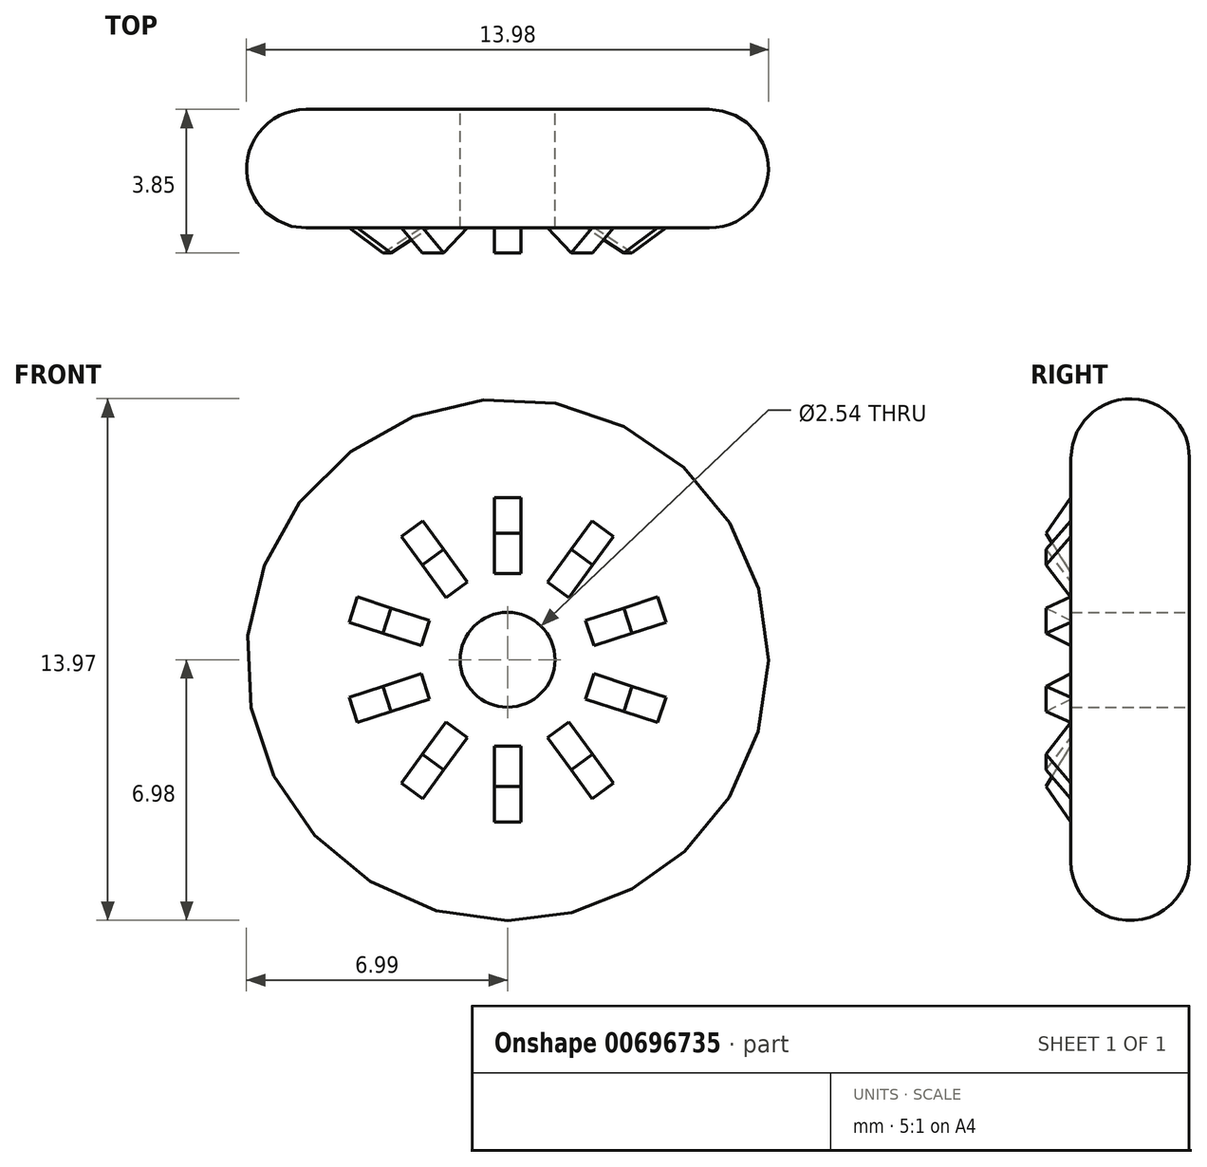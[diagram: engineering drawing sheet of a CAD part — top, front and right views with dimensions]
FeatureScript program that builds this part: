
annotation { "Feature Type Name" : "Feature", "Feature Type Description" : "" }
export const myFeature = defineFeature(function(context is Context, id is Id, definition is map)
    precondition{}
    {
        {
            var Q0;
            Q0=qCreatedBy(makeId("Front.planeOp"),FACE);
            var sketch = newSketch(context, id + "F0", { "sketchPlane" : qUnion([Q0])});
            skCircle(sketch, "E0", {"center": v(0, 0) * mm, "radius": 1.27 * mm});
            skCircle(sketch, "E1", {"center": v(0, 0) * mm, "radius": 6.99 * mm});
            skSolve(sketch);
        }
        {
            var Q0;
            Q0=makeQuery(id+"F0.imprint","IMPRINT",FACE,{"disambiguationData":[TD([[makeQuery(id+"F0.imprint","IMPRINT",EDGE,{"derivedFrom":sQuery(id+"F0.wireOp",EDGE,"E0")}),-1.0]])]});
            extrude(context, id + "F1", {"entities" : qUnion([Q0]), "endBound" : BoundingType.SYMMETRIC, "depth" : 3.17 * mm, "offsetDistance" : 25.4 * mm});
        }
        {
            var Q0;
            Q0=makeQuery(id+"F1.opExtrude","CAP_EDGE",EDGE,{"disambiguationData":[OSD([sQuery(id+"F0.wireOp",EDGE,"E1")])],"isStart":true});
            var Q1;
            Q1=makeQuery(id+"F1.opExtrude","CAP_EDGE",EDGE,{"disambiguationData":[OSD([sQuery(id+"F0.wireOp",EDGE,"E1")])],"isStart":false});
            fillet(context, id + "F2", {"entities" : qUnion([Q0, Q1]), "radius" : 1.59 * mm, "tangentPropagation" : true, "allowEdgeOverflow" : false});
        }
        {
            var Q0;
            Q0=qCreatedBy(makeId("Right.planeOp"),FACE);
            var sketch = newSketch(context, id + "F3", { "sketchPlane" : qUnion([Q0])});
            skLineSegment(sketch, "E2", {"start": v(-1.5, 4.48) * mm, "end": v(-2.26, 3.4) * mm});
            skLineSegment(sketch, "E3", {"start": v(-2.26, 3.4) * mm, "end": v(-1.58, 2.3) * mm});
            skLineSegment(sketch, "E4", {"start": v(-1.58, 2.3) * mm, "end": v(-1.5, 4.48) * mm});
            skPoint(sketch, "E5", {"position": v(-1.54, 3.4) * mm});
            skSolve(sketch);
        }
        {
            var Q0;
            Q0 = qSketchRegion(id + "F3", true);
            extrude(context, id + "F4", {"entities" : qUnion([Q0]), "operationType" : NewBodyOperationType.ADD, "endBound" : BoundingType.SYMMETRIC, "oppositeDirection" : true, "depth" : 0.71 * mm, "offsetDistance" : 25.4 * mm});
        }
        {
            var Q0;
            Q0=makeQuery(id+"F4.opExtrude","SWEPT_FACE",FACE,{"disambiguationData":[OSD([sQuery(id+"F3.wireOp",EDGE,"E2")])]});
            var Q1;
            Q1=makeQuery(id+"F4.opExtrude","CAP_FACE",FACE,{"disambiguationData":[OSD([sQuery(id+"F3.wireOp",EDGE,"E2"),sQuery(id+"F3.wireOp",EDGE,"E3"),sQuery(id+"F3.wireOp",EDGE,"E4")])],"isStart":true});
            var Q2;
            Q2=makeQuery(id+"F4.opExtrude","SWEPT_FACE",FACE,{"disambiguationData":[OSD([sQuery(id+"F3.wireOp",EDGE,"E3")])]});
            var Q3;
            Q3=makeQuery(id+"F4.opExtrude","CAP_FACE",FACE,{"disambiguationData":[OSD([sQuery(id+"F3.wireOp",EDGE,"E2"),sQuery(id+"F3.wireOp",EDGE,"E3"),sQuery(id+"F3.wireOp",EDGE,"E4")])],"isStart":false});
            var Q4;
            Q4=makeQuery(id+"F1.opExtrude","CAP_EDGE",EDGE,{"disambiguationData":[OSD([sQuery(id+"F0.wireOp",EDGE,"E0")])],"isStart":false});
            circularPattern(context, id + "F5", {"patternType" : PatternType.FACE, "faces" : qUnion([Q0, Q1, Q2, Q3]), "axis" : qUnion([Q4]), "angle" : 360 * degree, "instanceCount" : 10, "equalSpace" : true});
        }
    });
